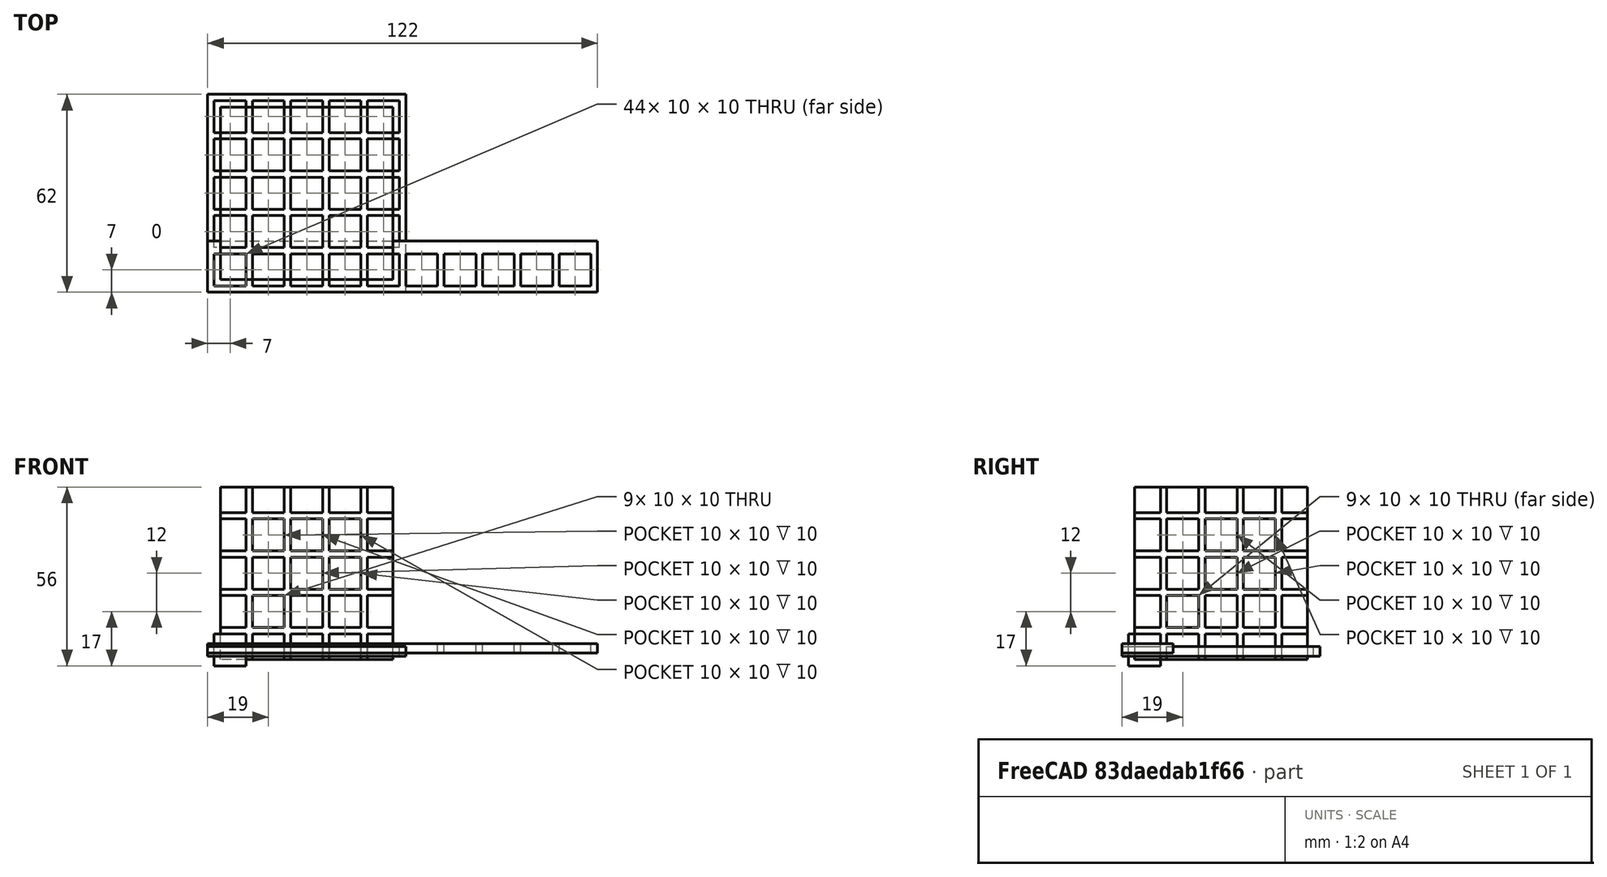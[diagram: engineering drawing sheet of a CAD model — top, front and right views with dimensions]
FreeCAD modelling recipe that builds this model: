
FCSTD DOCUMENT  (FreeCAD 1.0R39319 (Git))
Label: ojt1_t10p01_array
License: All rights reserved
LicenseURL: https://en.wikipedia.org/wiki/All_rights_reserved
objects: Part::Box×6, Part::FeaturePython×3, Part::Cut×3
note: 9 computed .brp shape members not serialized (recipe doc carries the construction recipe); baked Part::Feature solids carry a one-line shape summary decoded from their .brp

FEATURE [Part::Box] Box  label="muster cube"
  AttacherType = Attacher::AttachEngine3D
  Height = 10
  Length = 10
  Width = 10
FEATURE [Part::FeaturePython] Array  # Draft array (typed FeaturePython)
  AlwaysSyncPlacement = false
  Angle = 360
  ArrayType = 0
  Axis = (0,0,1)
  Base = -> Box
  Center = (0,0,0)
  Count = 10
  ExpandArray = false
  Fuse = false
  IntervalAxis = (0,0,0)
  IntervalX = (12,0,0)
  IntervalY = (0,100,0)
  IntervalZ = (0,0,100)
  NumberCircles = 3
  NumberPolar = 5
  NumberX = 10
  NumberY = 1
  NumberZ = 1
  PlacementList = 10 placements: arithmetic series from (0,0,0) step (12,0,0) to (108,0,0)
  RadialDistance = 50
  ScaleList = (10) [(1,1,1),(1,1,1),(1,1,1),(1,1,1),(1,1,1),(1,1,1),(1,1,1),(1,1,1),(1,1,1),(1,1,1)]
  Symmetry = 1
  TangentialDistance = 25
FEATURE [Part::Box] Box001  label="Cub001"
  AttacherType = Attacher::AttachEngine3D
  Height = 2
  Length = 12
  Placement = pos=(-2,-2,4) rot=(0,0,1;0rad)
  Width = 16
FEATURE [Part::Cut] Cut
  Base = -> Box001
  Refine = true
  Tool = -> Array
FEATURE [Part::Box] Box002  label="Cub"
  AttacherType = Attacher::AttachEngine3D
  Height = 10
  Length = 10
  Width = 10
FEATURE [Part::FeaturePython] Array001  # Draft array (typed FeaturePython)
  AlwaysSyncPlacement = false
  Angle = 360
  ArrayType = 0
  Axis = (0,0,1)
  Base = -> Box002
  Center = (0,0,0)
  Count = 25
  ExpandArray = false
  Fuse = false
  IntervalAxis = (0,0,0)
  IntervalX = (12,0,0)
  IntervalY = (0,12,0)
  IntervalZ = (0,0,100)
  NumberCircles = 3
  NumberPolar = 5
  NumberX = 5
  NumberY = 5
  NumberZ = 1
  PlacementList = 25 placements: [(0,0,0),(0,12,0),(0,24,0),(0,36,0),(0,48,0),(12,0,0),(12,12,0),(12,24,0),(12,36,0),(12,48,0),(24,0,0),(24,12,0),(24,24,0),(24,36,0),(24,48,0),(36,0,0),(36,12,0),(36,24,0),(36,36,0),(36,48,0),(48,0,0),(48,12,0),(48,24,0),(48,36,0),(48,48,0)]
  RadialDistance = 50
  ScaleList = (25) [(1,1,1),(1,1,1),(1,1,1),(1,1,1),(1,1,1),(1,1,1),(1,1,1),(1,1,1),(1,1,1),(1,1,1),(1,1,1),(1,1,1),(1,1,1),(1,1,1),(1,1,1),(1,1,1),(1,1,1),(1,1,1),+7 more]
  Symmetry = 1
  TangentialDistance = 25
FEATURE [Part::Box] Box003  label="Cub002"
  AttacherType = Attacher::AttachEngine3D
  Height = 3
  Length = 62
  Placement = pos=(-2,-2,3) rot=(0,0,1;0rad)
  Width = 62
FEATURE [Part::Cut] Cut001
  Base = -> Box003
  Refine = true
  Tool = -> Array001
FEATURE [Part::Box] Box004  label="Cub003"
  AttacherType = Attacher::AttachEngine3D
  Height = 10
  Length = 10
  Width = 10
FEATURE [Part::FeaturePython] Array002  # Draft array (typed FeaturePython)
  AlwaysSyncPlacement = false
  Angle = 360
  ArrayType = 0
  Axis = (0,0,1)
  Base = -> Box004
  Center = (0,0,0)
  Count = 125
  ExpandArray = false
  Fuse = false
  IntervalAxis = (0,0,0)
  IntervalX = (12,0,0)
  IntervalY = (0,12,0)
  IntervalZ = (0,0,12)
  NumberCircles = 3
  NumberPolar = 5
  NumberX = 5
  NumberY = 5
  NumberZ = 5
  PlacementList = 125 placements: [(0,0,0),(0,0,12),(0,0,24),(0,0,36),(0,0,48),(0,12,0),(0,12,12),(0,12,24),(0,12,36),(0,12,48),(0,24,0),(0,24,12),(0,24,24),(0,24,36),(0,24,48),(0,36,0),(0,36,12),(0,36,24),(0,36,36),(0,36,48),(0,48,0),(0,48,12),(0,48,24),(0,48,36),(0,48,48),(12,0,0),(12,0,12),(12,0,24),(12,0,36),(12,0,48),(12,12,0),(12,12,12),(12,12,24),(12,12,36),(12,12,48),(12,24,0),(12,24,12),(12,24,24),(12,24,36),(12,24,48),+85 more]
  RadialDistance = 50
  Symmetry = 1
  TangentialDistance = 25
FEATURE [Part::Box] Box005  label="Cub004"
  AttacherType = Attacher::AttachEngine3D
  Height = 54
  Length = 54
  Placement = pos=(2,2,2) rot=(0,0,1;0rad)
  Width = 54
FEATURE [Part::Cut] Cut002
  Base = -> Box005
  Refine = true
  Tool = -> Array002
